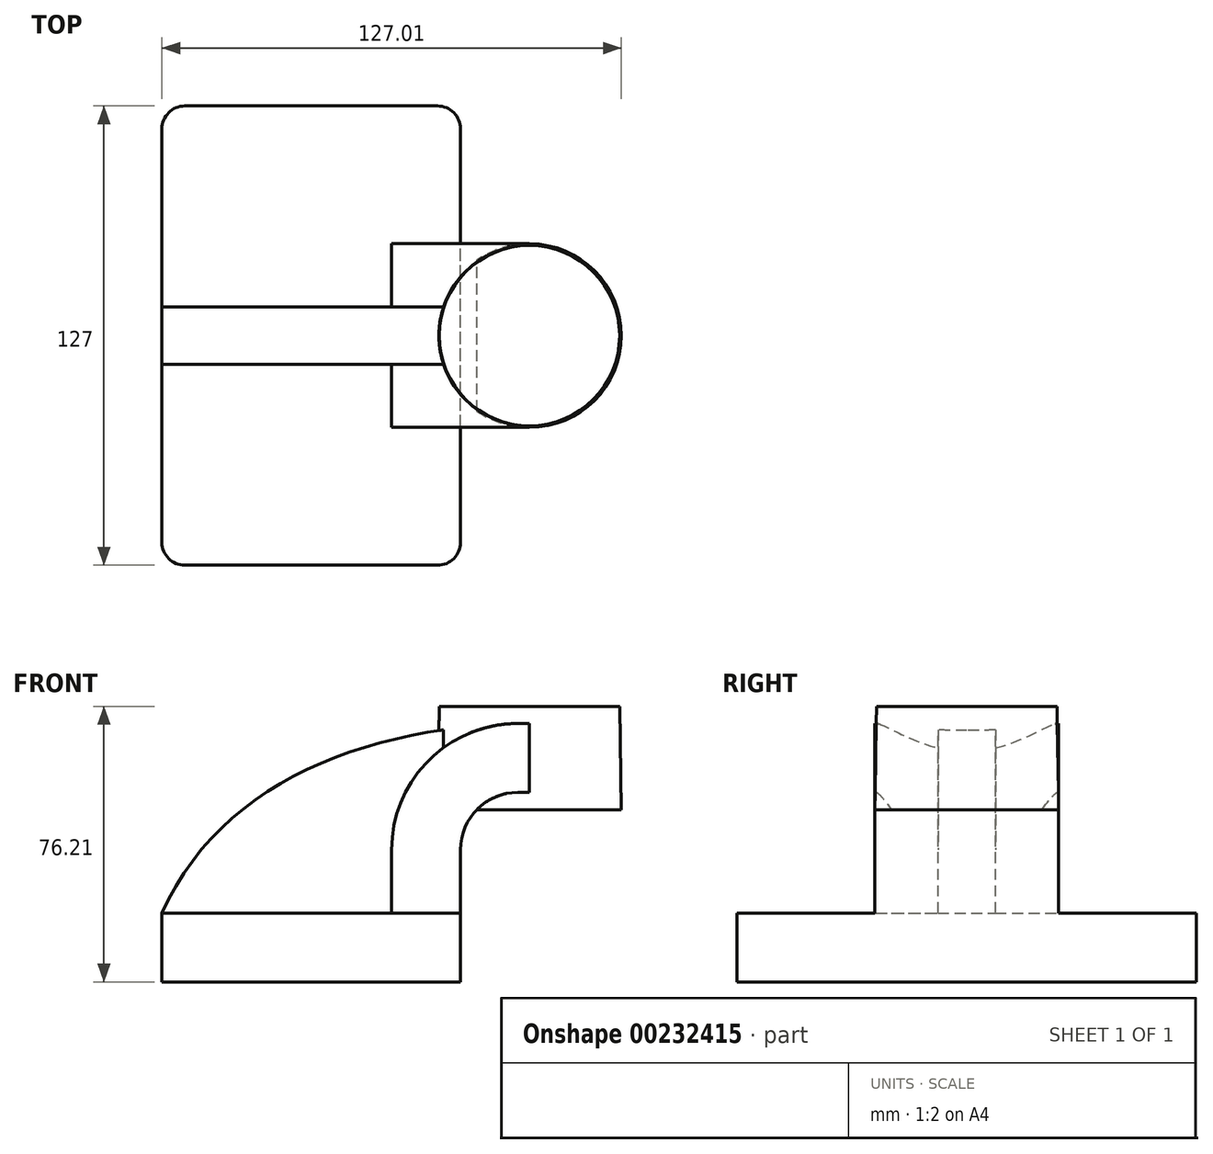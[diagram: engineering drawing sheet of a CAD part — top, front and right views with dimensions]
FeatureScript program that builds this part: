
annotation { "Feature Type Name" : "Feature", "Feature Type Description" : "" }
export const myFeature = defineFeature(function(context is Context, id is Id, definition is map)
    precondition{}
    {
        {
            var Q0;
            Q0=qCreatedBy(makeId("Front.planeOp"),FACE);
            var sketch = newSketch(context, id + "F0", { "sketchPlane" : qUnion([Q0])});
            skLineSegment(sketch, "E0.bottom", {"start": v(-41.28, -9.53) * mm, "end": v(41.28, -9.53) * mm});
            skLineSegment(sketch, "E0.top", {"start": v(-41.28, 9.53) * mm, "end": v(41.28, 9.53) * mm});
            skLineSegment(sketch, "E0.left", {"start": v(-41.28, -9.53) * mm, "end": v(-41.28, 9.53) * mm});
            skLineSegment(sketch, "E0.right", {"start": v(41.28, -9.53) * mm, "end": v(41.28, 9.53) * mm});
            skPoint(sketch, "E0.middle", {"position": v(0, 0) * mm});
            skLineSegment(sketch, "E1.bottom", {"start": v(60.33, 38.1) * mm, "end": v(111.12, 38.1) * mm});
            skLineSegment(sketch, "E1.top", {"start": v(60.32, 66.67) * mm, "end": v(111.12, 66.67) * mm});
            skLineSegment(sketch, "E1.left", {"start": v(60.33, 38.1) * mm, "end": v(60.33, 66.67) * mm});
            skLineSegment(sketch, "E1.right", {"start": v(111.12, 38.1) * mm, "end": v(111.12, 66.67) * mm});
            skPoint(sketch, "E1.middle", {"position": v(85.72, 52.39) * mm});
            skLineSegment(sketch, "E2", {"start": v(41.28, 9.52) * mm, "end": v(41.28, 27) * mm});
            skArc(sketch, "E3", {"start": v(41.27, 27) * mm, "mid": v(45.92, 38.23) * mm, "end": v(57.15, 42.88) * mm});
            skLineSegment(sketch, "E4", {"start": v(57.15, 42.88) * mm, "end": v(85.25, 42.88) * mm});
            skLineSegment(sketch, "E5.0", {"start": v(57.15, 61.93) * mm, "end": v(85.25, 61.93) * mm});
            skArc(sketch, "E5.1", {"start": v(22.22, 27) * mm, "mid": v(32.45, 51.7) * mm, "end": v(57.15, 61.93) * mm});
            skLineSegment(sketch, "E5.2", {"start": v(22.22, 9.52) * mm, "end": v(22.22, 27) * mm});
            skLineSegment(sketch, "E6", {"start": v(85.72, 38.1) * mm, "end": v(85.25, 66.67) * mm});
            skFitSpline(sketch, "E7", {"points": [v(-41.28, 9.53) * mm, v(57.15, 61.93) * mm], "startDerivative": vector(48.01, 107.29) * mm, "endDerivative": vector(129.71, 3.91) * mm});
            skSolve(sketch);
        }
        {
            var Q0;
            Q0=makeQuery(id+"F0.imprint","IMPRINT",FACE,{"disambiguationData":[TD([[makeQuery(id+"F0.imprint","IMPRINT",EDGE,{"derivedFrom":sQuery(id+"F0.wireOp",EDGE,"E0.bottom")}),1.0]])]});
            extrude(context, id + "F1", {"entities" : qUnion([Q0]), "endBound" : BoundingType.SYMMETRIC, "depth" : 127 * mm});
        }
        {
            var Q0;
            {var subQ1=sQuery(id+"F0.wireOp",EDGE,"E2");Q0=makeQuery(id+"F0.imprint","IMPRINT",FACE,{"disambiguationData":[TD([[makeQuery(id+"F0.imprint","IMPRINT",EDGE,{"derivedFrom":subQ1}),1.0]])]});}
            extrude(context, id + "F2", {"entities" : qUnion([Q0]), "operationType" : NewBodyOperationType.ADD, "endBound" : BoundingType.SYMMETRIC, "depth" : 50.8 * mm});
        }
        {
            var Q0;
            {var subQ3=sQuery(id+"F0.wireOp",EDGE,"E5.2");Q0=makeQuery(id+"F0.imprint","IMPRINT",FACE,{"disambiguationData":[TD([[makeQuery(id+"F0.imprint","IMPRINT",EDGE,{"derivedFrom":subQ3}),1.0]])]});}
            extrude(context, id + "F3", {"entities" : qUnion([Q0]), "operationType" : NewBodyOperationType.ADD, "endBound" : BoundingType.SYMMETRIC, "depth" : 15.88 * mm});
        }
        {
            var Q0;
            {var subQ7=sQuery(id+"F0.wireOp",EDGE,"E6");Q0=makeQuery(id+"F0.imprint","IMPRINT",FACE,{"disambiguationData":[TD([[makeQuery(id+"F0.imprint","IMPRINT",EDGE,{"derivedFrom":subQ7}),1.0]])]});}
            var Q1;
            Q1=sQuery(id+"F0.wireOp",EDGE,"E1.left");
            revolve(context, id + "F4", {"operationType" : NewBodyOperationType.ADD, "entities" : qUnion([Q0]), "axis" : qUnion([Q1]), "revolveType" : RevolveType.FULL});
        }
        {
            var Q0;
            Q0=makeQuery(id+"F1.opExtrude","CAP_EDGE",EDGE,{"disambiguationData":[OSD([sQuery(id+"F0.wireOp",EDGE,"E0.left")])],"isStart":false});
            var Q1;
            Q1=makeQuery(id+"F1.opExtrude","CAP_EDGE",EDGE,{"disambiguationData":[OSD([sQuery(id+"F0.wireOp",EDGE,"E0.right")])],"isStart":false});
            var Q2;
            Q2=makeQuery(id+"F1.opExtrude","CAP_EDGE",EDGE,{"disambiguationData":[OSD([sQuery(id+"F0.wireOp",EDGE,"E0.right")])],"isStart":true});
            var Q3;
            Q3=makeQuery(id+"F1.opExtrude","CAP_EDGE",EDGE,{"disambiguationData":[OSD([sQuery(id+"F0.wireOp",EDGE,"E0.left")])],"isStart":true});
            fillet(context, id + "F5", {"entities" : qUnion([Q0, Q1, Q2, Q3]), "radius" : 6.35 * mm, "tangentPropagation" : true, "allowEdgeOverflow" : false});
        }
    });
